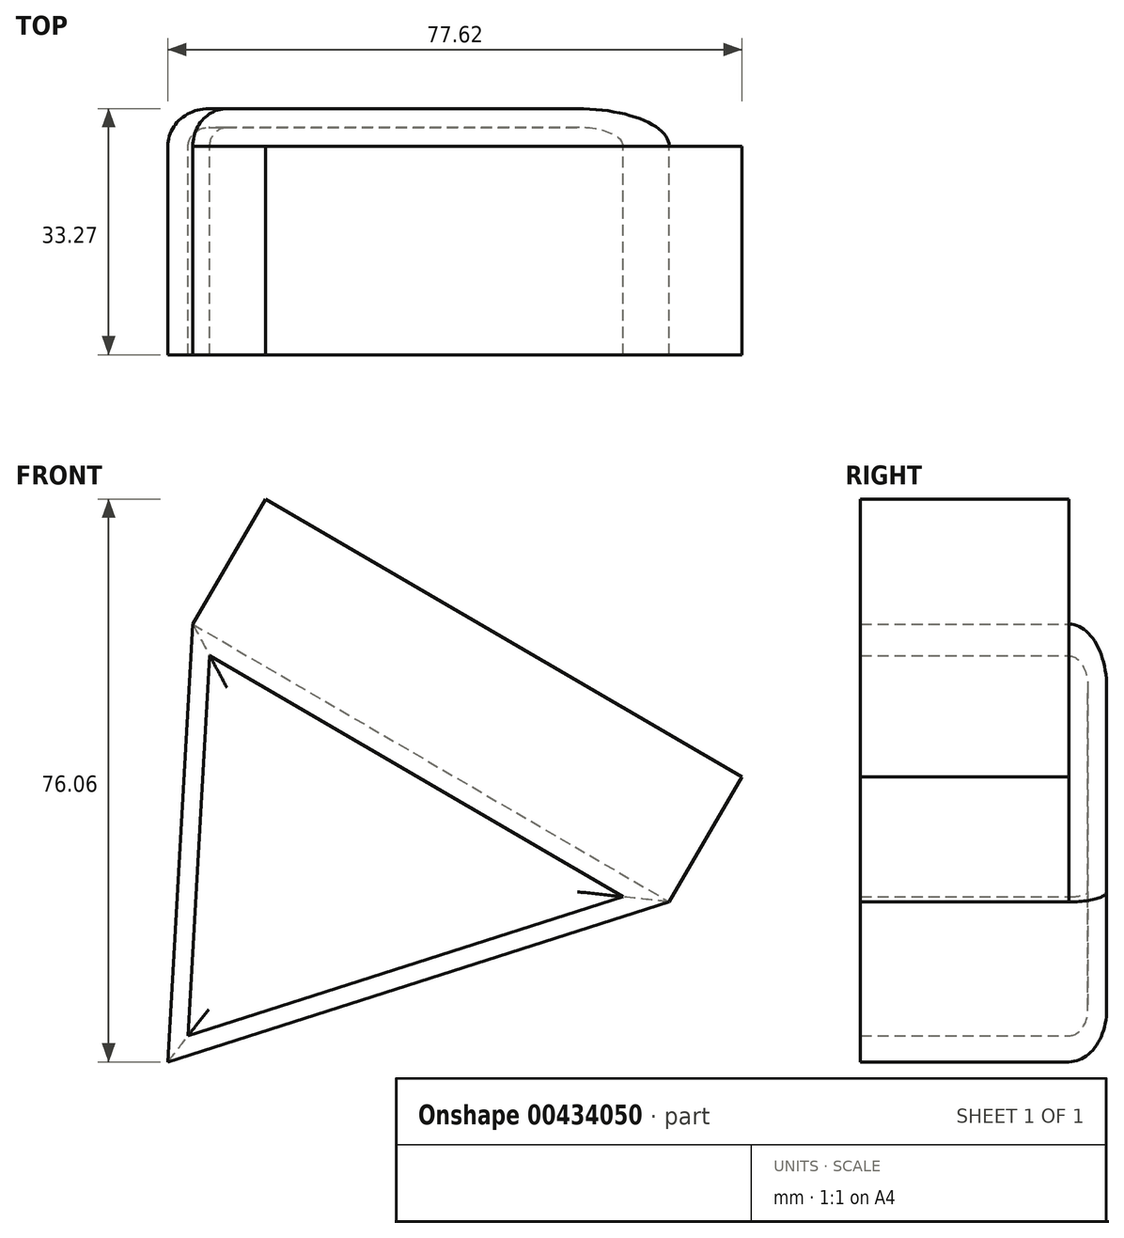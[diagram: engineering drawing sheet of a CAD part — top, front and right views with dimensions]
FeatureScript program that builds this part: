
annotation { "Feature Type Name" : "Feature", "Feature Type Description" : "" }
export const myFeature = defineFeature(function(context is Context, id is Id, definition is map)
    precondition{}
    {
        {
            var Q0;
            Q0=qCreatedBy(makeId("Front.planeOp"),FACE);
            var sketch = newSketch(context, id + "F0", { "sketchPlane" : qUnion([Q0])});
            skLineSegment(sketch, "E0", {"start": v(-64.4, 54.56) * mm, "end": v(0, 17.03) * mm});
            skLineSegment(sketch, "E1", {"start": v(-64.4, 54.56) * mm, "end": v(-67.77, -4.6) * mm});
            skLineSegment(sketch, "E2", {"start": v(0, 17.03) * mm, "end": v(-67.77, -4.6) * mm});
            skCircle(sketch, "E3", {"center": v(-48.26, 22.22) * mm, "radius": 10.62 * mm});
            skSolve(sketch);
        }
        {
            var Q0;
            Q0=makeQuery(id+"F0.imprint","IMPRINT",FACE,{"disambiguationData":[TD([[makeQuery(id+"F0.imprint","IMPRINT",EDGE,{"derivedFrom":sQuery(id+"F0.wireOp",EDGE,"E0")}),-1.0]])]});
            var Q1;
            Q1=makeQuery(id+"F0.imprint","IMPRINT",FACE,{"disambiguationData":[TD([[makeQuery(id+"F0.imprint","IMPRINT",EDGE,{"derivedFrom":sQuery(id+"F0.wireOp",EDGE,"E3")}),1.0]])]});
            extrude(context, id + "F1", {"entities" : qUnion([Q0, Q1]), "depth" : 33.27 * mm});
        }
        {
            var Q0;
            Q0=sQuery(id+"F0.wireOp",EDGE,"E3");
            extrude(context, id + "F2", {"bodyType" : ToolBodyType.SURFACE, "surfaceEntities" : qUnion([Q0]), "oppositeDirection" : true, "depth" : 95.5 * mm});
        }
        {
            var Q0;
            Q0=makeQuery(id+"F2.opExtrude","SWEPT_FACE",FACE,{"disambiguationData":[OSD([sQuery(id+"F0.wireOp",EDGE,"E3")])]});
            var Q1;
            Q1=makeQuery(id+"F1.opExtrude","CAP_EDGE",EDGE,{"disambiguationData":[OSD([sQuery(id+"F0.wireOp",EDGE,"E2")])],"isStart":true});
            var Q2;
            Q2=makeQuery(id+"F1.opExtrude","CAP_EDGE",EDGE,{"disambiguationData":[OSD([sQuery(id+"F0.wireOp",EDGE,"E0")])],"isStart":true});
            var Q3;
            Q3=makeQuery(id+"F1.opExtrude","CAP_EDGE",EDGE,{"disambiguationData":[OSD([sQuery(id+"F0.wireOp",EDGE,"E1")])],"isStart":true});
            fillet(context, id + "F3", {"entities" : qUnion([Q0, Q1, Q2, Q3]), "radius" : 5.08 * mm, "tangentPropagation" : true, "allowEdgeOverflow" : false});
        }
        {
            var Q0;
            Q0=makeQuery(id+"F1.opExtrude","CAP_FACE",FACE,{"disambiguationData":[OSD([sQuery(id+"F0.wireOp",EDGE,"E0"),sQuery(id+"F0.wireOp",EDGE,"E1"),sQuery(id+"F0.wireOp",EDGE,"E2")])],"isStart":false});
            shell(context, id + "F4", {"entities" : qUnion([Q0]), "thickness" : 2.54 * mm});
        }
        {
            var Q0;
            Q0=makeQuery(id+"F1.opExtrude","SWEPT_FACE",FACE,{"disambiguationData":[OSD([sQuery(id+"F0.wireOp",EDGE,"E0")])]});
            extrude(context, id + "F5", {"entities" : qUnion([Q0]), "operationType" : NewBodyOperationType.ADD, "depth" : 19.56 * mm});
        }
    });
